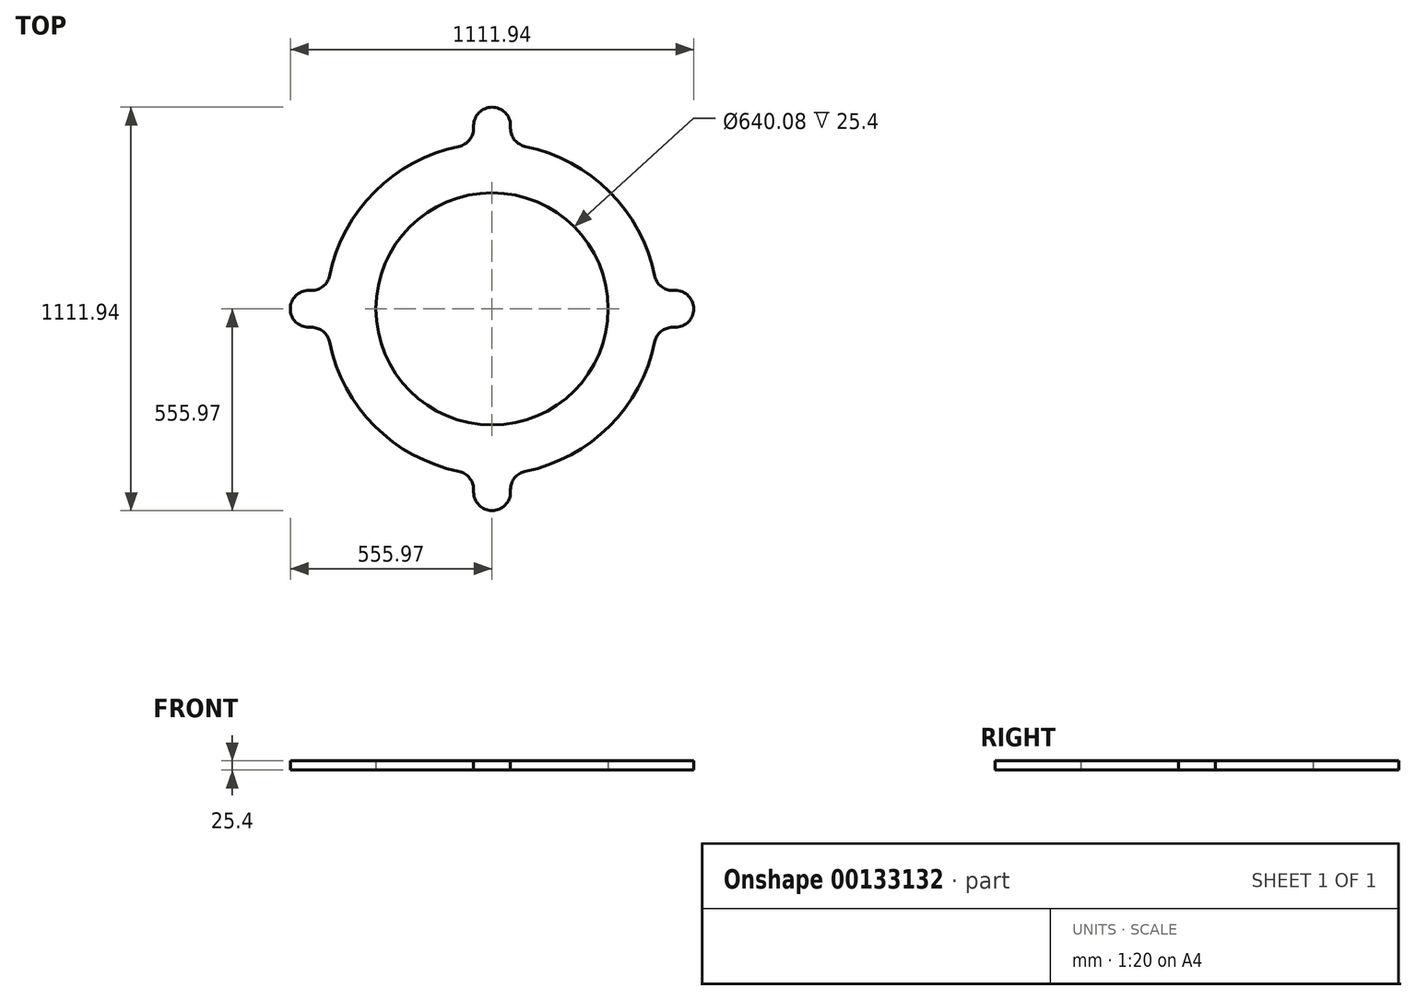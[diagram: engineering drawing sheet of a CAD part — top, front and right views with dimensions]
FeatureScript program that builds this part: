
annotation { "Feature Type Name" : "Feature", "Feature Type Description" : "" }
export const myFeature = defineFeature(function(context is Context, id is Id, definition is map)
    precondition{}
    {
        {
            var Q0;
            Q0=qCreatedBy(makeId("Top.planeOp"),FACE);
            var sketch = newSketch(context, id + "F0", { "sketchPlane" : qUnion([Q0])});
            skArc(sketch, "E0", {"start": v(-50.8, 454.37) * mm, "mid": v(-323.29, 323.29) * mm, "end": v(-454.37, 50.8) * mm});
            skLineSegment(sketch, "E1.bottom", {"start": v(454.37, -50.8) * mm, "end": v(555.97, -50.8) * mm});
            skLineSegment(sketch, "E1.top", {"start": v(454.37, 50.8) * mm, "end": v(555.97, 50.8) * mm});
            skLineSegment(sketch, "E1.left", {"start": v(454.37, -50.8) * mm, "end": v(454.37, 50.8) * mm, "construction": true});
            skLineSegment(sketch, "E1.right", {"start": v(555.97, -50.8) * mm, "end": v(555.97, 50.8) * mm});
            skLineSegment(sketch, "E2", {"start": v(-457.2, 0) * mm, "end": v(457.2, 0) * mm, "construction": true});
            skPoint(sketch, "E2.endSnap0", {"position": v(454.37, 0) * mm});
            skLineSegment(sketch, "E3", {"start": v(0, -457.2) * mm, "end": v(0, 457.2) * mm, "construction": true});
            skLineSegment(sketch, "E4.bottom", {"start": v(-50.8, 454.37) * mm, "end": v(50.8, 454.37) * mm, "construction": true});
            skLineSegment(sketch, "E4.top", {"start": v(-50.8, 555.97) * mm, "end": v(50.8, 555.97) * mm});
            skLineSegment(sketch, "E4.left", {"start": v(-50.8, 454.37) * mm, "end": v(-50.8, 555.97) * mm});
            skLineSegment(sketch, "E4.right", {"start": v(50.8, 454.37) * mm, "end": v(50.8, 555.97) * mm});
            skLineSegment(sketch, "E5.bottom", {"start": v(-50.8, -454.37) * mm, "end": v(50.8, -454.37) * mm, "construction": true});
            skLineSegment(sketch, "E5.top", {"start": v(-50.8, -555.97) * mm, "end": v(50.8, -555.97) * mm});
            skLineSegment(sketch, "E5.left", {"start": v(-50.8, -454.37) * mm, "end": v(-50.8, -555.97) * mm});
            skLineSegment(sketch, "E5.right", {"start": v(50.8, -454.37) * mm, "end": v(50.8, -555.97) * mm});
            skLineSegment(sketch, "E6.bottom", {"start": v(-454.37, -50.8) * mm, "end": v(-555.97, -50.8) * mm});
            skLineSegment(sketch, "E6.top", {"start": v(-454.37, 50.8) * mm, "end": v(-555.97, 50.8) * mm});
            skLineSegment(sketch, "E6.left", {"start": v(-454.37, -50.8) * mm, "end": v(-454.37, 50.8) * mm, "construction": true});
            skLineSegment(sketch, "E6.right", {"start": v(-555.97, -50.8) * mm, "end": v(-555.97, 50.8) * mm});
            skArc(sketch, "E7.trimOffspring", {"start": v(454.37, 50.8) * mm, "mid": v(323.29, 323.29) * mm, "end": v(50.8, 454.37) * mm});
            skArc(sketch, "E8.trimOffspring", {"start": v(50.8, -454.37) * mm, "mid": v(323.29, -323.29) * mm, "end": v(454.37, -50.8) * mm});
            skArc(sketch, "E9.trimOffspring", {"start": v(-454.37, -50.8) * mm, "mid": v(-323.29, -323.29) * mm, "end": v(-50.8, -454.37) * mm});
            skCircle(sketch, "E10", {"center": v(0, 0) * mm, "radius": 320.04 * mm});
            skLineSegment(sketch, "E11", {"start": v(454.37, 50.8) * mm, "end": v(555.97, -50.8) * mm, "construction": true});
            skLineSegment(sketch, "E12", {"start": v(555.97, 50.8) * mm, "end": v(454.37, -50.8) * mm, "construction": true});
            skLineSegment(sketch, "E13", {"start": v(-50.8, 555.97) * mm, "end": v(50.8, 454.37) * mm, "construction": true});
            skLineSegment(sketch, "E14", {"start": v(-50.8, 454.37) * mm, "end": v(50.8, 555.97) * mm, "construction": true});
            skLineSegment(sketch, "E15", {"start": v(-555.97, 50.8) * mm, "end": v(-454.37, -50.8) * mm, "construction": true});
            skLineSegment(sketch, "E16", {"start": v(-454.37, 50.8) * mm, "end": v(-555.97, -50.8) * mm, "construction": true});
            skLineSegment(sketch, "E17", {"start": v(50.8, -555.97) * mm, "end": v(-50.8, -454.37) * mm, "construction": true});
            skLineSegment(sketch, "E18", {"start": v(-50.8, -555.97) * mm, "end": v(50.8, -454.37) * mm, "construction": true});
            skSolve(sketch);
        }
        {
            var Q0;
            Q0 = qSketchRegion(id + "F0", true);
            extrude(context, id + "F1", {"entities" : qUnion([Q0]), "depth" : 25.4 * mm});
        }
        {
            var Q0;
            Q0=makeQuery(id+"F1.opExtrude","SWEPT_EDGE",EDGE,{"disambiguationData":[OSD([sQuery(id+"F0.wireOp",EDGE,"E5.top"),sQuery(id+"F0.wireOp",EDGE,"E5.right")])]});
            var Q1;
            Q1=makeQuery(id+"F1.opExtrude","SWEPT_EDGE",EDGE,{"disambiguationData":[OSD([sQuery(id+"F0.wireOp",EDGE,"E5.top"),sQuery(id+"F0.wireOp",EDGE,"E5.left")])]});
            var Q2;
            Q2=makeQuery(id+"F1.opExtrude","SWEPT_EDGE",EDGE,{"disambiguationData":[OSD([sQuery(id+"F0.wireOp",EDGE,"E1.bottom"),sQuery(id+"F0.wireOp",EDGE,"E1.right")])]});
            var Q3;
            Q3=makeQuery(id+"F1.opExtrude","SWEPT_EDGE",EDGE,{"disambiguationData":[OSD([sQuery(id+"F0.wireOp",EDGE,"E1.top"),sQuery(id+"F0.wireOp",EDGE,"E1.right")])]});
            var Q4;
            Q4=makeQuery(id+"F1.opExtrude","SWEPT_EDGE",EDGE,{"disambiguationData":[OSD([sQuery(id+"F0.wireOp",EDGE,"E4.top"),sQuery(id+"F0.wireOp",EDGE,"E4.right")])]});
            var Q5;
            Q5=makeQuery(id+"F1.opExtrude","SWEPT_EDGE",EDGE,{"disambiguationData":[OSD([sQuery(id+"F0.wireOp",EDGE,"E4.top"),sQuery(id+"F0.wireOp",EDGE,"E4.left")])]});
            var Q6;
            Q6=makeQuery(id+"F1.opExtrude","SWEPT_EDGE",EDGE,{"disambiguationData":[OSD([sQuery(id+"F0.wireOp",EDGE,"E6.top"),sQuery(id+"F0.wireOp",EDGE,"E6.right")])]});
            var Q7;
            Q7=makeQuery(id+"F1.opExtrude","SWEPT_EDGE",EDGE,{"disambiguationData":[OSD([sQuery(id+"F0.wireOp",EDGE,"E6.bottom"),sQuery(id+"F0.wireOp",EDGE,"E6.right")])]});
            var Q8;
            Q8=makeQuery(id+"F1.opExtrude","SWEPT_EDGE",EDGE,{"disambiguationData":[OSD([sQuery(id+"F0.wireOp",EDGE,"E5.right"),sQuery(id+"F0.wireOp",EDGE,"E8.trimOffspring")])]});
            var Q9;
            Q9=makeQuery(id+"F1.opExtrude","SWEPT_EDGE",EDGE,{"disambiguationData":[OSD([sQuery(id+"F0.wireOp",EDGE,"E1.bottom"),sQuery(id+"F0.wireOp",EDGE,"E8.trimOffspring")])]});
            var Q10;
            Q10=makeQuery(id+"F1.opExtrude","SWEPT_EDGE",EDGE,{"disambiguationData":[OSD([sQuery(id+"F0.wireOp",EDGE,"E1.top"),sQuery(id+"F0.wireOp",EDGE,"E7.trimOffspring")])]});
            var Q11;
            Q11=makeQuery(id+"F1.opExtrude","SWEPT_EDGE",EDGE,{"disambiguationData":[OSD([sQuery(id+"F0.wireOp",EDGE,"E4.right"),sQuery(id+"F0.wireOp",EDGE,"E7.trimOffspring")])]});
            var Q12;
            Q12=makeQuery(id+"F1.opExtrude","SWEPT_EDGE",EDGE,{"disambiguationData":[OSD([sQuery(id+"F0.wireOp",EDGE,"E0"),sQuery(id+"F0.wireOp",EDGE,"E4.left")])]});
            var Q13;
            Q13=makeQuery(id+"F1.opExtrude","SWEPT_EDGE",EDGE,{"disambiguationData":[OSD([sQuery(id+"F0.wireOp",EDGE,"E0"),sQuery(id+"F0.wireOp",EDGE,"E6.top")])]});
            var Q14;
            Q14=makeQuery(id+"F1.opExtrude","SWEPT_EDGE",EDGE,{"disambiguationData":[OSD([sQuery(id+"F0.wireOp",EDGE,"E6.bottom"),sQuery(id+"F0.wireOp",EDGE,"E9.trimOffspring")])]});
            var Q15;
            Q15=makeQuery(id+"F1.opExtrude","SWEPT_EDGE",EDGE,{"disambiguationData":[OSD([sQuery(id+"F0.wireOp",EDGE,"E5.left"),sQuery(id+"F0.wireOp",EDGE,"E9.trimOffspring")])]});
            fillet(context, id + "F2", {"entities" : qUnion([Q0, Q1, Q2, Q3, Q4, Q5, Q6, Q7, Q8, Q9, Q10, Q11, Q12, Q13, Q14, Q15]), "radius" : 50.8 * mm, "tangentPropagation" : true, "allowEdgeOverflow" : false});
        }
    });
